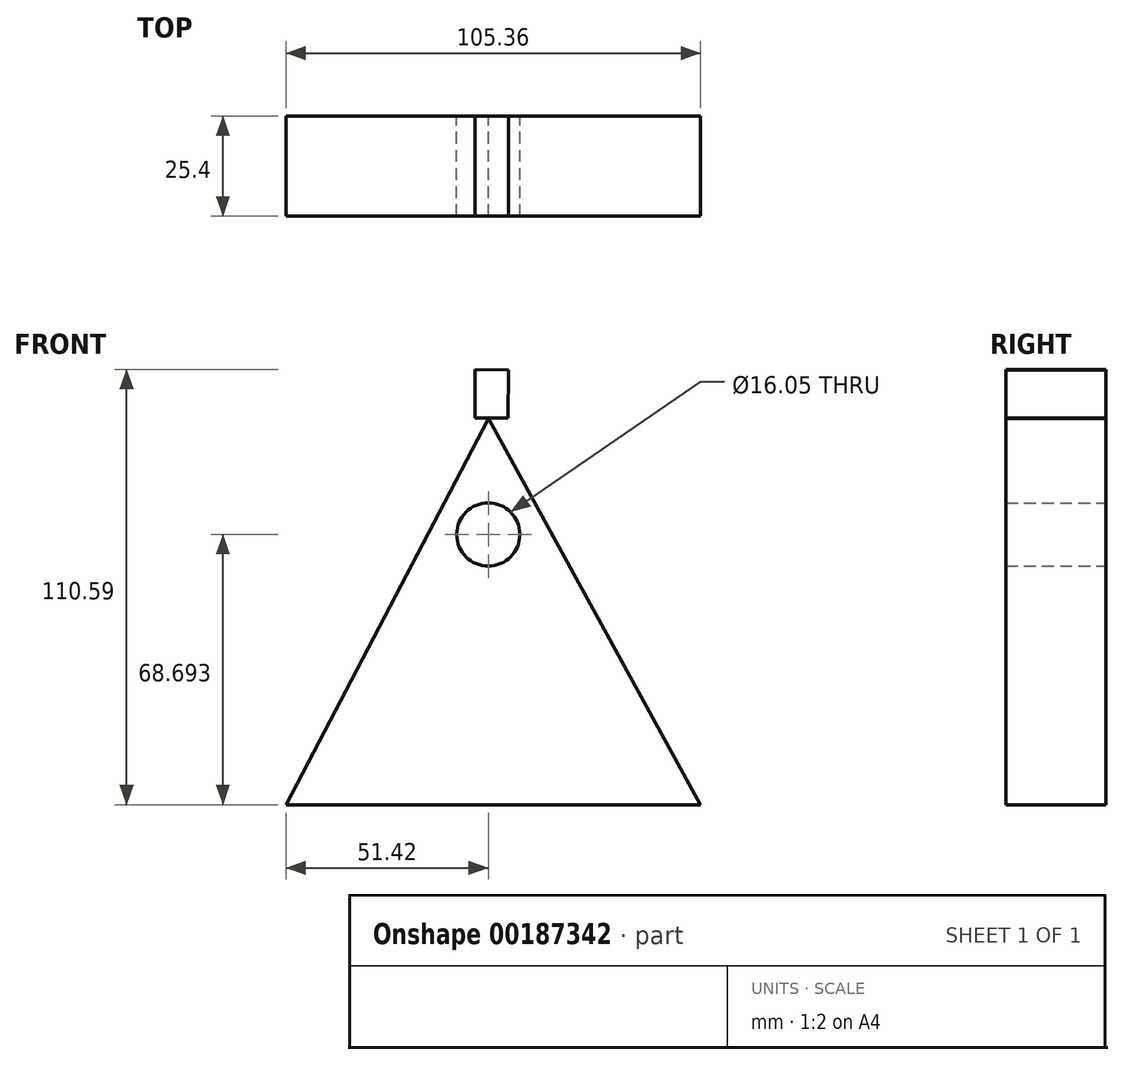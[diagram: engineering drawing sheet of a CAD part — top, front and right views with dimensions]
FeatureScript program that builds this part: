
annotation { "Feature Type Name" : "Feature", "Feature Type Description" : "" }
export const myFeature = defineFeature(function(context is Context, id is Id, definition is map)
    precondition{}
    {
        {
            var Q0;
            Q0=qCreatedBy(makeId("Front.planeOp"),FACE);
            var sketch = newSketch(context, id + "F0", { "sketchPlane" : qUnion([Q0])});
            skLineSegment(sketch, "E0", {"start": v(-51.42, -51.95) * mm, "end": v(53.94, -51.95) * mm});
            skLineSegment(sketch, "E1", {"start": v(53.94, -51.95) * mm, "end": v(0, 46.26) * mm});
            skLineSegment(sketch, "E2", {"start": v(0, 46.26) * mm, "end": v(-51.42, -51.95) * mm});
            skCircle(sketch, "E3", {"center": v(0, 16.74) * mm, "radius": 8.03 * mm});
            skLineSegment(sketch, "E4", {"start": v(-6.35, 46.4) * mm, "end": v(8.07, 46.26) * mm});
            skLineSegment(sketch, "E5", {"start": v(5.03, 46.29) * mm, "end": v(5.14, 58.56) * mm});
            skLineSegment(sketch, "E6", {"start": v(5.14, 58.56) * mm, "end": v(-3.43, 58.64) * mm});
            skLineSegment(sketch, "E7", {"start": v(-3.43, 58.64) * mm, "end": v(-3.43, 46.36) * mm});
            skLineSegment(sketch, "E8", {"start": v(23.6, 3.28) * mm, "end": v(53.47, 3.28) * mm});
            skLineSegment(sketch, "E9", {"start": v(53.47, 3.28) * mm, "end": v(53.47, 9.33) * mm});
            skLineSegment(sketch, "E10", {"start": v(53.47, 9.33) * mm, "end": v(53.47, 3.28) * mm});
            skLineSegment(sketch, "E11", {"start": v(53.47, 3.28) * mm, "end": v(61.15, 3.28) * mm});
            skLineSegment(sketch, "E12", {"start": v(61.15, 3.28) * mm, "end": v(53.47, 3.28) * mm});
            skLineSegment(sketch, "E13", {"start": v(53.47, 3.28) * mm, "end": v(53.47, -3.64) * mm});
            skLineSegment(sketch, "E14", {"start": v(-22.66, 2.98) * mm, "end": v(-53.6, 2.98) * mm});
            skLineSegment(sketch, "E15", {"start": v(-53.6, 2.98) * mm, "end": v(-53.6, 9.2) * mm});
            skLineSegment(sketch, "E16", {"start": v(-53.6, 9.2) * mm, "end": v(-53.6, -4.43) * mm});
            skLineSegment(sketch, "E17", {"start": v(-53.6, -4.43) * mm, "end": v(-53.6, 2.98) * mm});
            skLineSegment(sketch, "E18", {"start": v(-57.97, 2.98) * mm, "end": v(-53.6, 2.98) * mm});
            skLineSegment(sketch, "E19", {"start": v(-40.77, -51.95) * mm, "end": v(-40.77, -73.4) * mm});
            skLineSegment(sketch, "E20", {"start": v(-40.77, -73.4) * mm, "end": v(-31.9, -73.4) * mm});
            skLineSegment(sketch, "E21", {"start": v(-31.9, -73.4) * mm, "end": v(-48.05, -73.4) * mm});
            skLineSegment(sketch, "E22", {"start": v(-48.05, -73.4) * mm, "end": v(-40.77, -73.4) * mm});
            skLineSegment(sketch, "E23", {"start": v(-40.77, -73.4) * mm, "end": v(-40.77, -76.97) * mm});
            skLineSegment(sketch, "E24", {"start": v(71.08, 19.79) * mm, "end": v(60.1, 19.79) * mm});
            skLineSegment(sketch, "E25", {"start": v(60.1, 19.79) * mm, "end": v(60.1, -4.7) * mm});
            skLineSegment(sketch, "E26", {"start": v(32.7, -53.4) * mm, "end": v(32.7, -74.05) * mm});
            skLineSegment(sketch, "E27", {"start": v(32.7, -74.05) * mm, "end": v(47.65, -74.05) * mm});
            skLineSegment(sketch, "E28", {"start": v(47.65, -74.05) * mm, "end": v(15.35, -74.05) * mm});
            skLineSegment(sketch, "E29", {"start": v(15.35, -74.05) * mm, "end": v(32.7, -74.05) * mm});
            skLineSegment(sketch, "E30", {"start": v(32.7, -74.05) * mm, "end": v(32.7, -78.95) * mm});
            skSolve(sketch);
        }
        {
            var Q0;
            Q0 = qSketchRegion(id + "F0", true);
            extrude(context, id + "F1", {"entities" : qUnion([Q0]), "depth" : 25.4 * mm});
        }
    });
